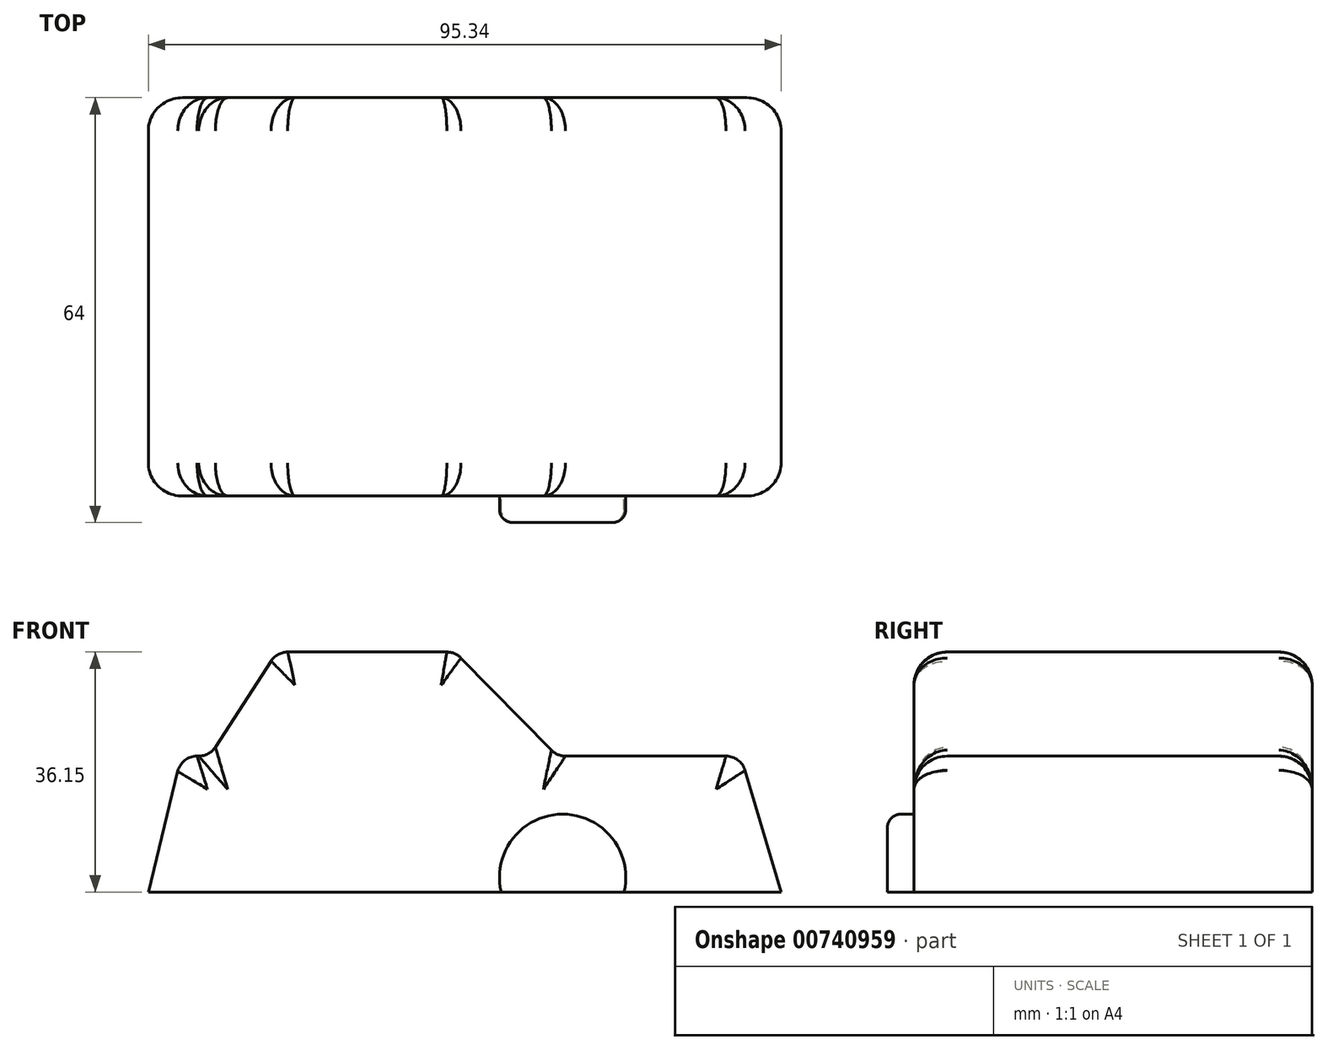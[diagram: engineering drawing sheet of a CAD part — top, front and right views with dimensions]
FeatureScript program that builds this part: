
annotation { "Feature Type Name" : "Feature", "Feature Type Description" : "" }
export const myFeature = defineFeature(function(context is Context, id is Id, definition is map)
    precondition{}
    {
        {
            var Q0;
            Q0=qCreatedBy(makeId("Front.planeOp"),FACE);
            var sketch = newSketch(context, id + "F0", { "sketchPlane" : qUnion([Q0])});
            skLineSegment(sketch, "E0.bottom", {"start": v(-46.22, 0) * mm, "end": v(49.12, 0) * mm});
            skLineSegment(sketch, "E0.top", {"start": v(-41.24, 20.47) * mm, "end": v(43.04, 20.47) * mm});
            skLineSegment(sketch, "E1.bottom", {"start": v(-37, 20.47) * mm, "end": v(15.38, 20.47) * mm});
            skLineSegment(sketch, "E1.top", {"start": v(-26.86, 36.15) * mm, "end": v(0, 36.15) * mm});
            skLineSegment(sketch, "E2", {"start": v(-37, 20.47) * mm, "end": v(-26.86, 36.15) * mm});
            skLineSegment(sketch, "E3", {"start": v(-46.22, 0) * mm, "end": v(-41.24, 20.47) * mm});
            skLineSegment(sketch, "E4", {"start": v(49.12, 0) * mm, "end": v(43.04, 20.47) * mm});
            skLineSegment(sketch, "E5", {"start": v(15.38, 20.47) * mm, "end": v(0, 36.15) * mm});
            skSolve(sketch);
        }
        {
            var Q0;
            Q0 = qSketchRegion(id + "F0", true);
            extrude(context, id + "F1", {"entities" : qUnion([Q0]), "depth" : 60 * mm, "offsetDistance" : 25.4 * mm});
        }
        {
            var Q0;
            {var subQ0=sQuery(id+"F0.wireOp",EDGE,"E0.top");Q0=makeQuery(id+"F1.opExtrude","CAP_EDGE",EDGE,{"disambiguationData":[OSD([subQ0]),TDD([makeQuery(id+"F0.imprint","IMPRINT",EDGE,{"disambiguationData":[TD([[makeQuery(id+"F0.imprint","INTERSECT",VERTEX,{"derivedFrom":[subQ0,sQuery(id+"F0.wireOp",EDGE,"E4")]}),1.0]])],"derivedFrom":subQ0})])],"isStart":true});}
            var Q1;
            Q1=makeQuery(id+"F1.opExtrude","CAP_EDGE",EDGE,{"disambiguationData":[OSD([sQuery(id+"F0.wireOp",EDGE,"E4")])],"isStart":true});
            var Q2;
            Q2=makeQuery(id+"F1.opExtrude","CAP_EDGE",EDGE,{"disambiguationData":[OSD([sQuery(id+"F0.wireOp",EDGE,"E5")])],"isStart":true});
            var Q3;
            Q3=makeQuery(id+"F1.opExtrude","CAP_EDGE",EDGE,{"disambiguationData":[OSD([sQuery(id+"F0.wireOp",EDGE,"E1.top")])],"isStart":true});
            var Q4;
            Q4=makeQuery(id+"F1.opExtrude","CAP_EDGE",EDGE,{"disambiguationData":[OSD([sQuery(id+"F0.wireOp",EDGE,"E2")])],"isStart":true});
            var Q5;
            {var subQ0=sQuery(id+"F0.wireOp",EDGE,"E0.top");Q5=makeQuery(id+"F1.opExtrude","CAP_EDGE",EDGE,{"disambiguationData":[OSD([subQ0]),TDD([makeQuery(id+"F0.imprint","IMPRINT",EDGE,{"disambiguationData":[TD([[makeQuery(id+"F0.imprint","INTERSECT",VERTEX,{"derivedFrom":[subQ0,sQuery(id+"F0.wireOp",EDGE,"E3")]}),-1.0]])],"derivedFrom":subQ0})])],"isStart":true});}
            var Q6;
            Q6=makeQuery(id+"F1.opExtrude","CAP_EDGE",EDGE,{"disambiguationData":[OSD([sQuery(id+"F0.wireOp",EDGE,"E3")])],"isStart":true});
            var Q7;
            Q7=makeQuery(id+"F1.opExtrude","CAP_EDGE",EDGE,{"disambiguationData":[OSD([sQuery(id+"F0.wireOp",EDGE,"E3")])],"isStart":false});
            var Q8;
            {var subQ0=sQuery(id+"F0.wireOp",EDGE,"E0.top");Q8=makeQuery(id+"F1.opExtrude","CAP_EDGE",EDGE,{"disambiguationData":[OSD([subQ0]),TDD([makeQuery(id+"F0.imprint","IMPRINT",EDGE,{"disambiguationData":[TD([[makeQuery(id+"F0.imprint","INTERSECT",VERTEX,{"derivedFrom":[subQ0,sQuery(id+"F0.wireOp",EDGE,"E3")]}),-1.0]])],"derivedFrom":subQ0})])],"isStart":false});}
            var Q9;
            Q9=makeQuery(id+"F1.opExtrude","CAP_EDGE",EDGE,{"disambiguationData":[OSD([sQuery(id+"F0.wireOp",EDGE,"E2")])],"isStart":false});
            var Q10;
            Q10=makeQuery(id+"F1.opExtrude","CAP_EDGE",EDGE,{"disambiguationData":[OSD([sQuery(id+"F0.wireOp",EDGE,"E1.top")])],"isStart":false});
            var Q11;
            Q11=makeQuery(id+"F1.opExtrude","CAP_EDGE",EDGE,{"disambiguationData":[OSD([sQuery(id+"F0.wireOp",EDGE,"E5")])],"isStart":false});
            var Q12;
            {var subQ0=sQuery(id+"F0.wireOp",EDGE,"E0.top");Q12=makeQuery(id+"F1.opExtrude","CAP_EDGE",EDGE,{"disambiguationData":[OSD([subQ0]),TDD([makeQuery(id+"F0.imprint","IMPRINT",EDGE,{"disambiguationData":[TD([[makeQuery(id+"F0.imprint","INTERSECT",VERTEX,{"derivedFrom":[subQ0,sQuery(id+"F0.wireOp",EDGE,"E4")]}),1.0]])],"derivedFrom":subQ0})])],"isStart":false});}
            var Q13;
            Q13=makeQuery(id+"F1.opExtrude","CAP_EDGE",EDGE,{"disambiguationData":[OSD([sQuery(id+"F0.wireOp",EDGE,"E4")])],"isStart":false});
            fillet(context, id + "F2", {"entities" : qUnion([Q0, Q1, Q2, Q3, Q4, Q5, Q6, Q7, Q8, Q9, Q10, Q11, Q12, Q13]), "radius" : 5 * mm, "tangentPropagation" : true, "allowEdgeOverflow" : false});
        }
        {
            var Q0;
            Q0=makeQuery(id+"F1.opExtrude","SWEPT_EDGE",EDGE,{"disambiguationData":[OSD([sQuery(id+"F0.wireOp",EDGE,"E0.top"),sQuery(id+"F0.wireOp",EDGE,"E3")])]});
            var Q1;
            Q1=makeQuery(id+"F1.opExtrude","SWEPT_EDGE",EDGE,{"disambiguationData":[OSD([sQuery(id+"F0.wireOp",EDGE,"E0.top"),sQuery(id+"F0.wireOp",EDGE,"E1.bottom"),sQuery(id+"F0.wireOp",EDGE,"E2")])]});
            var Q2;
            Q2=makeQuery(id+"F1.opExtrude","SWEPT_EDGE",EDGE,{"disambiguationData":[OSD([sQuery(id+"F0.wireOp",EDGE,"E1.top"),sQuery(id+"F0.wireOp",EDGE,"E2")])]});
            var Q3;
            Q3=makeQuery(id+"F1.opExtrude","SWEPT_EDGE",EDGE,{"disambiguationData":[OSD([sQuery(id+"F0.wireOp",EDGE,"E1.top"),sQuery(id+"F0.wireOp",EDGE,"E5")])]});
            var Q4;
            Q4=makeQuery(id+"F1.opExtrude","SWEPT_EDGE",EDGE,{"disambiguationData":[OSD([sQuery(id+"F0.wireOp",EDGE,"E0.top"),sQuery(id+"F0.wireOp",EDGE,"E4")])]});
            var Q5;
            Q5=makeQuery(id+"F1.opExtrude","SWEPT_EDGE",EDGE,{"disambiguationData":[OSD([sQuery(id+"F0.wireOp",EDGE,"E0.top"),sQuery(id+"F0.wireOp",EDGE,"E1.bottom"),sQuery(id+"F0.wireOp",EDGE,"E5")])]});
            fillet(context, id + "F3", {"entities" : qUnion([Q0, Q1, Q2, Q3, Q4, Q5]), "radius" : 3 * mm, "tangentPropagation" : true, "allowEdgeOverflow" : false});
        }
        {
            var Q0;
            Q0=makeQuery(id+"F1.opExtrude","CAP_FACE",FACE,{"disambiguationData":[OSD([sQuery(id+"F0.wireOp",EDGE,"E0.bottom"),sQuery(id+"F0.wireOp",EDGE,"E0.top"),sQuery(id+"F0.wireOp",EDGE,"E1.top"),sQuery(id+"F0.wireOp",EDGE,"E2"),sQuery(id+"F0.wireOp",EDGE,"E3"),sQuery(id+"F0.wireOp",EDGE,"E4"),sQuery(id+"F0.wireOp",EDGE,"E5")])],"isStart":false});
            var sketch = newSketch(context, id + "F4", { "sketchPlane" : qUnion([Q0])});
            skArc(sketch, "E6", {"start": v(25.46, 0) * mm, "mid": v(16.2, 11.72) * mm, "end": v(6.93, 0) * mm});
            skSolve(sketch);
        }
        {
            var Q0;
            {var subQ0=sQuery(id+"F4.wireOp",EDGE,"E6");Q0=makeQuery(id+"F4.imprint","IMPRINT",FACE,{"disambiguationData":[TD([[makeQuery(id+"F4.imprint","IMPRINT",EDGE,{"derivedFrom":subQ0}),1.0]])]});}
            extrude(context, id + "F5", {"entities" : qUnion([Q0]), "operationType" : NewBodyOperationType.ADD, "depth" : 4 * mm, "offsetDistance" : 25 * mm});
        }
        {
            var Q0;
            Q0=makeQuery(id+"F5.opExtrude","CAP_EDGE",EDGE,{"disambiguationData":[OSD([sQuery(id+"F4.wireOp",EDGE,"E6")])],"isStart":true});
            var Q1;
            Q1=makeQuery(id+"F5.opExtrude","CAP_EDGE",EDGE,{"disambiguationData":[OSD([sQuery(id+"F4.wireOp",EDGE,"E6")])],"isStart":false});
            fillet(context, id + "F6", {"entities" : qUnion([Q0, Q1]), "radius" : 2 * mm, "tangentPropagation" : true, "allowEdgeOverflow" : false});
        }
    });
